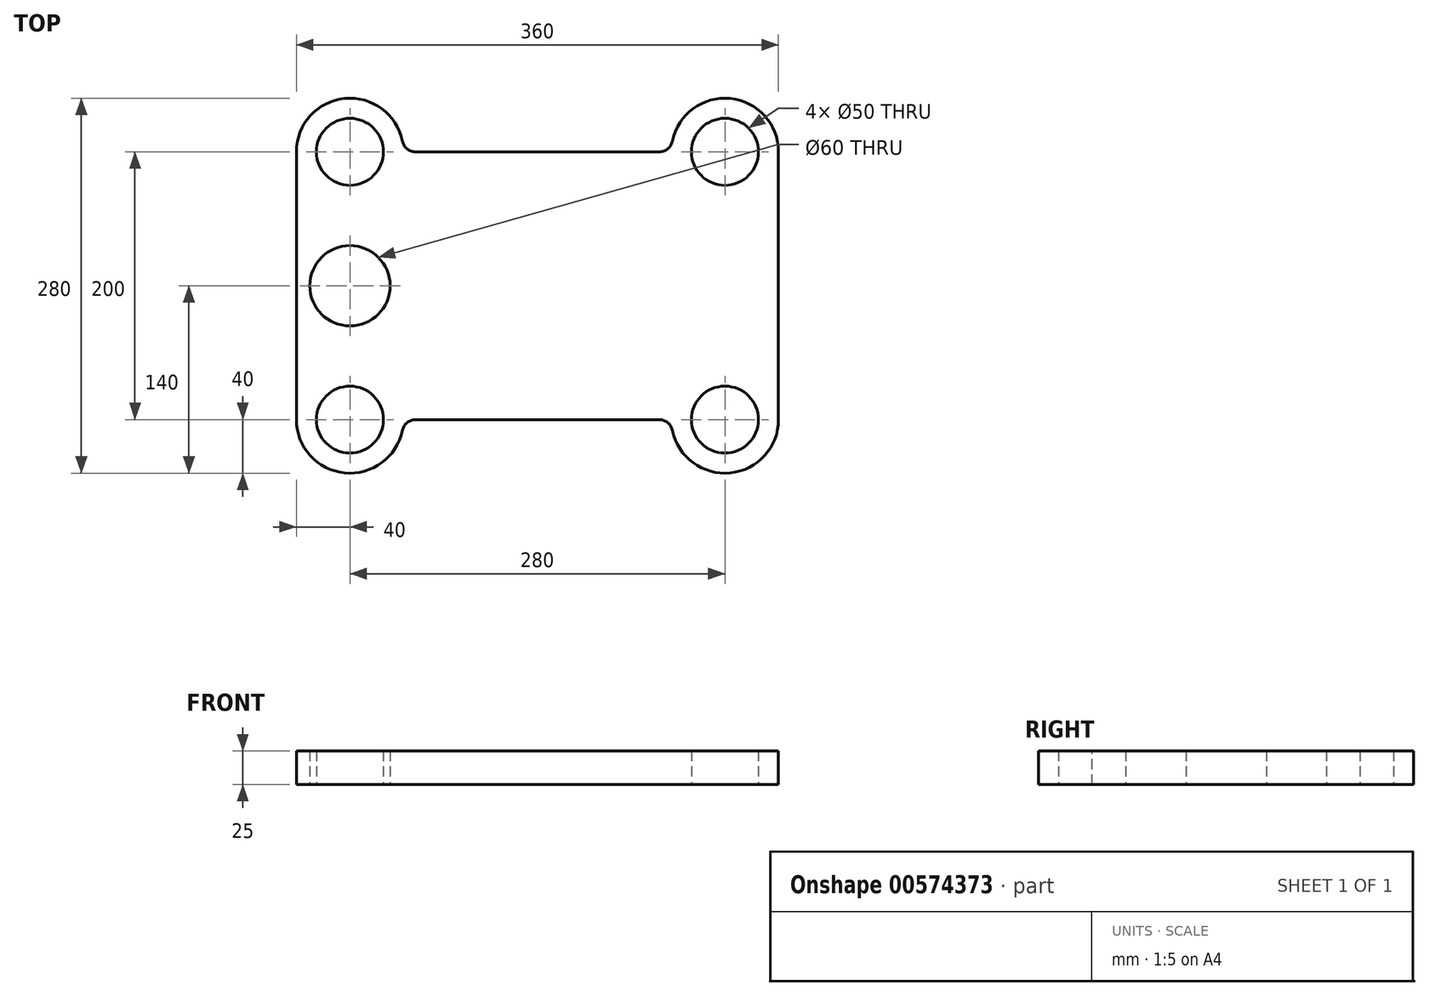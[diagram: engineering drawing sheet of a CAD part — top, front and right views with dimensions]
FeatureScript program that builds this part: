
annotation { "Feature Type Name" : "Feature", "Feature Type Description" : "" }
export const myFeature = defineFeature(function(context is Context, id is Id, definition is map)
    precondition{}
    {
        {
            var Q0;
            Q0=qCreatedBy(makeId("Top.planeOp"),FACE);
            var sketch = newSketch(context, id + "F0", { "sketchPlane" : qUnion([Q0])});
            skLineSegment(sketch, "E0", {"start": v(-140, 140.97) * mm, "end": v(-140, -153.08) * mm, "construction": true});
            skLineSegment(sketch, "E1", {"start": v(140, 154.94) * mm, "end": v(140, -153.08) * mm, "construction": true});
            skCircle(sketch, "E2", {"center": v(-140, 100) * mm, "radius": 40 * mm});
            skCircle(sketch, "E3", {"center": v(-140, -100) * mm, "radius": 40 * mm});
            skCircle(sketch, "E4", {"center": v(140, 100) * mm, "radius": 40 * mm});
            skCircle(sketch, "E5", {"center": v(140, -100) * mm, "radius": 40 * mm});
            skLineSegment(sketch, "E6", {"start": v(-100, 100) * mm, "end": v(100, 100) * mm});
            skLineSegment(sketch, "E7", {"start": v(-100, -100) * mm, "end": v(100, -100) * mm});
            skLineSegment(sketch, "E8", {"start": v(180, 100) * mm, "end": v(180, -100) * mm});
            skLineSegment(sketch, "E9", {"start": v(-180, 100) * mm, "end": v(-180, -100) * mm});
            skCircle(sketch, "E10", {"center": v(-140, 0) * mm, "radius": 30 * mm});
            skCircle(sketch, "E11", {"center": v(-140, 100) * mm, "radius": 25 * mm});
            skCircle(sketch, "E12", {"center": v(140, 100) * mm, "radius": 25 * mm});
            skCircle(sketch, "E13", {"center": v(140, -100) * mm, "radius": 25 * mm});
            skCircle(sketch, "E14", {"center": v(-140, -100) * mm, "radius": 25 * mm});
            skSolve(sketch);
        }
        {
            var Q0;
            {var subQ0=sQuery(id+"F0.wireOp",EDGE,"E6");Q0=makeQuery(id+"F0.imprint","IMPRINT",FACE,{"disambiguationData":[TD([[makeQuery(id+"F0.imprint","IMPRINT",EDGE,{"derivedFrom":subQ0}),-1.0]])]});}
            var Q1;
            Q1=makeQuery(id+"F0.imprint","IMPRINT",FACE,{"disambiguationData":[TD([[makeQuery(id+"F0.imprint","IMPRINT",EDGE,{"derivedFrom":sQuery(id+"F0.wireOp",EDGE,"E11")}),-1.0]])]});
            var Q2;
            Q2=makeQuery(id+"F0.imprint","IMPRINT",FACE,{"disambiguationData":[TD([[makeQuery(id+"F0.imprint","IMPRINT",EDGE,{"derivedFrom":sQuery(id+"F0.wireOp",EDGE,"E12")}),-1.0]])]});
            var Q3;
            Q3=makeQuery(id+"F0.imprint","IMPRINT",FACE,{"disambiguationData":[TD([[makeQuery(id+"F0.imprint","IMPRINT",EDGE,{"derivedFrom":sQuery(id+"F0.wireOp",EDGE,"E13")}),-1.0]])]});
            var Q4;
            Q4=makeQuery(id+"F0.imprint","IMPRINT",FACE,{"disambiguationData":[TD([[makeQuery(id+"F0.imprint","IMPRINT",EDGE,{"derivedFrom":sQuery(id+"F0.wireOp",EDGE,"E14")}),-1.0]])]});
            extrude(context, id + "F1", {"entities" : qUnion([Q0, Q1, Q2, Q3, Q4]), "depth" : 25 * mm, "offsetDistance" : 25 * mm});
        }
        {
            var Q0;
            Q0=makeQuery(id+"F1.opExtrude","SWEPT_EDGE",EDGE,{"disambiguationData":[OSD([sQuery(id+"F0.wireOp",EDGE,"E3"),sQuery(id+"F0.wireOp",EDGE,"E7")])]});
            var Q1;
            Q1=makeQuery(id+"F1.opExtrude","SWEPT_EDGE",EDGE,{"disambiguationData":[OSD([sQuery(id+"F0.wireOp",EDGE,"E5"),sQuery(id+"F0.wireOp",EDGE,"E7")])]});
            var Q2;
            Q2=makeQuery(id+"F1.opExtrude","SWEPT_EDGE",EDGE,{"disambiguationData":[OSD([sQuery(id+"F0.wireOp",EDGE,"E2"),sQuery(id+"F0.wireOp",EDGE,"E6")])]});
            var Q3;
            Q3=makeQuery(id+"F1.opExtrude","SWEPT_EDGE",EDGE,{"disambiguationData":[OSD([sQuery(id+"F0.wireOp",EDGE,"E4"),sQuery(id+"F0.wireOp",EDGE,"E6")])]});
            fillet(context, id + "F2", {"entities" : qUnion([Q0, Q1, Q2, Q3]), "radius" : 10 * mm, "tangentPropagation" : true, "allowEdgeOverflow" : false});
        }
    });
